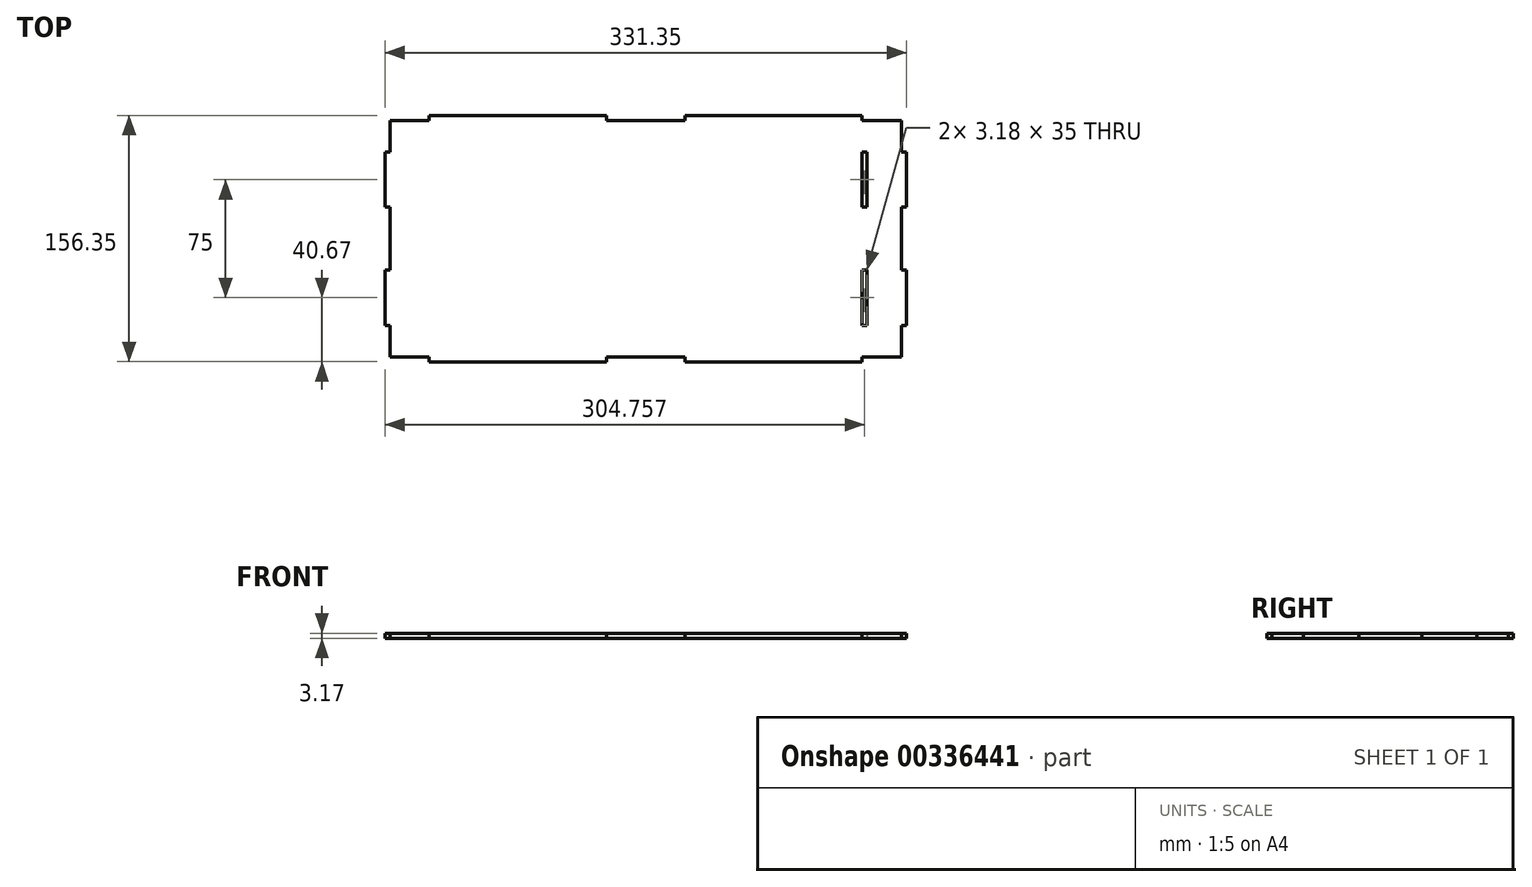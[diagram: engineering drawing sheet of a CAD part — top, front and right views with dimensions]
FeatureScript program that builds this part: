
annotation { "Feature Type Name" : "Feature", "Feature Type Description" : "" }
export const myFeature = defineFeature(function(context is Context, id is Id, definition is map)
    precondition{}
    {
        {
            var Q0;
            Q0=qCreatedBy(makeId("Top.planeOp"),FACE);
            var sketch = newSketch(context, id + "F0", { "sketchPlane" : qUnion([Q0])});
            skLineSegment(sketch, "E0", {"start": v(0, 0) * mm, "end": v(0, 150) * mm, "construction": true});
            skLineSegment(sketch, "E1", {"start": v(0, 150) * mm, "end": v(325, 150) * mm, "construction": true});
            skLineSegment(sketch, "E2", {"start": v(325, 150) * mm, "end": v(325, 0) * mm, "construction": true});
            skLineSegment(sketch, "E3", {"start": v(325, 0) * mm, "end": v(0, 0) * mm, "construction": true});
            skLineSegment(sketch, "E4", {"start": v(162.5, 150) * mm, "end": v(162.5, 0) * mm, "construction": true});
            skLineSegment(sketch, "E5", {"start": v(162.5, 0) * mm, "end": v(137.5, 0) * mm});
            skLineSegment(sketch, "E6", {"start": v(137.5, 0) * mm, "end": v(137.5, -3.18) * mm});
            skLineSegment(sketch, "E7", {"start": v(137.5, -3.18) * mm, "end": v(25, -3.18) * mm});
            skLineSegment(sketch, "E8", {"start": v(25, -3.18) * mm, "end": v(25, 0) * mm});
            skLineSegment(sketch, "E9", {"start": v(25, 0) * mm, "end": v(0, 0) * mm});
            skLineSegment(sketch, "E10", {"start": v(0, 20) * mm, "end": v(-3.18, 20) * mm});
            skLineSegment(sketch, "E11", {"start": v(-3.18, 20) * mm, "end": v(-3.18, 55) * mm});
            skLineSegment(sketch, "E12", {"start": v(-3.18, 55) * mm, "end": v(0, 55) * mm});
            skLineSegment(sketch, "E13", {"start": v(0, 75) * mm, "end": v(162.5, 75) * mm, "construction": true});
            skLineSegment(sketch, "E14.MirrorCS", {"start": v(0, 130) * mm, "end": v(-3.18, 130) * mm});
            skLineSegment(sketch, "E15.MirrorCS", {"start": v(-3.18, 95) * mm, "end": v(0, 95) * mm});
            skLineSegment(sketch, "E16.MirrorCS", {"start": v(137.5, 150) * mm, "end": v(137.5, 153.18) * mm});
            skLineSegment(sketch, "E17.MirrorCS", {"start": v(25, 153.18) * mm, "end": v(25, 150) * mm});
            skLineSegment(sketch, "E18.MirrorCS", {"start": v(25, 150) * mm, "end": v(0, 150) * mm});
            skLineSegment(sketch, "E19.MirrorCS", {"start": v(137.5, 153.18) * mm, "end": v(25, 153.18) * mm});
            skLineSegment(sketch, "E20.MirrorCS", {"start": v(-3.18, 130) * mm, "end": v(-3.18, 95) * mm});
            skLineSegment(sketch, "E21.MirrorCS", {"start": v(162.5, 150) * mm, "end": v(137.5, 150) * mm});
            skLineSegment(sketch, "E22", {"start": v(0, 95) * mm, "end": v(0, 55) * mm});
            skLineSegment(sketch, "E23", {"start": v(0, 150) * mm, "end": v(0, 130) * mm});
            skLineSegment(sketch, "E24", {"start": v(0, 20) * mm, "end": v(0, 0) * mm});
            skLineSegment(sketch, "E25.MirrorCS", {"start": v(187.5, 150) * mm, "end": v(187.5, 153.18) * mm});
            skLineSegment(sketch, "E26.MirrorCS", {"start": v(187.5, 0) * mm, "end": v(187.5, -3.18) * mm});
            skLineSegment(sketch, "E27.MirrorCS", {"start": v(300, -3.18) * mm, "end": v(300, 0) * mm});
            skLineSegment(sketch, "E28.MirrorCS", {"start": v(325, 20) * mm, "end": v(328.18, 20) * mm});
            skLineSegment(sketch, "E29.MirrorCS", {"start": v(300, 153.18) * mm, "end": v(300, 150) * mm});
            skLineSegment(sketch, "E30.MirrorCS", {"start": v(328.18, 55) * mm, "end": v(325, 55) * mm});
            skLineSegment(sketch, "E31.MirrorCS", {"start": v(328.18, 95) * mm, "end": v(325, 95) * mm});
            skLineSegment(sketch, "E32.MirrorCS", {"start": v(325, 130) * mm, "end": v(328.18, 130) * mm});
            skLineSegment(sketch, "E33.MirrorCS", {"start": v(300, 0) * mm, "end": v(325, 0) * mm});
            skLineSegment(sketch, "E34.MirrorCS", {"start": v(325, 20) * mm, "end": v(325, 0) * mm});
            skLineSegment(sketch, "E35.MirrorCS", {"start": v(187.5, -3.18) * mm, "end": v(300, -3.18) * mm});
            skLineSegment(sketch, "E36.MirrorCS", {"start": v(328.18, 20) * mm, "end": v(328.18, 55) * mm});
            skLineSegment(sketch, "E37.MirrorCS", {"start": v(162.5, 150) * mm, "end": v(187.5, 150) * mm});
            skLineSegment(sketch, "E38.MirrorCS", {"start": v(162.5, 0) * mm, "end": v(187.5, 0) * mm});
            skLineSegment(sketch, "E39.MirrorCS", {"start": v(187.5, 153.18) * mm, "end": v(300, 153.18) * mm});
            skLineSegment(sketch, "E40.MirrorCS", {"start": v(0, 0) * mm, "end": v(325, 0) * mm, "construction": true});
            skLineSegment(sketch, "E41.MirrorCS", {"start": v(325, 95) * mm, "end": v(325, 55) * mm});
            skLineSegment(sketch, "E42.MirrorCS", {"start": v(325, 75) * mm, "end": v(162.5, 75) * mm, "construction": true});
            skLineSegment(sketch, "E43.MirrorCS", {"start": v(325, 150) * mm, "end": v(0, 150) * mm, "construction": true});
            skLineSegment(sketch, "E44.MirrorCS", {"start": v(325, 150) * mm, "end": v(325, 130) * mm});
            skLineSegment(sketch, "E45.MirrorCS", {"start": v(300, 150) * mm, "end": v(325, 150) * mm});
            skLineSegment(sketch, "E46.MirrorCS", {"start": v(325, 0) * mm, "end": v(325, 150) * mm, "construction": true});
            skLineSegment(sketch, "E47.MirrorCS", {"start": v(328.18, 130) * mm, "end": v(328.18, 95) * mm});
            skLineSegment(sketch, "E48.1.0.0", {"start": v(303.17, 130) * mm, "end": v(303.17, 95) * mm});
            skLineSegment(sketch, "E48.1.0.2", {"start": v(303.17, 20) * mm, "end": v(303.17, 55) * mm});
            skLineSegment(sketch, "E48.1.0.3", {"start": v(300, 75) * mm, "end": v(137.5, 75) * mm, "construction": true});
            skLineSegment(sketch, "E48.1.0.4", {"start": v(300, 150) * mm, "end": v(300, 0) * mm, "construction": true});
            skLineSegment(sketch, "E48.1.0.6", {"start": v(300, 130) * mm, "end": v(303.18, 130) * mm});
            skLineSegment(sketch, "E48.1.0.7", {"start": v(300, 20) * mm, "end": v(300, 0) * mm, "construction": true});
            skLineSegment(sketch, "E48.1.0.8", {"start": v(303.18, 95) * mm, "end": v(300, 95) * mm});
            skLineSegment(sketch, "E48.1.0.10", {"start": v(300, 20) * mm, "end": v(303.18, 20) * mm});
            skLineSegment(sketch, "E48.1.0.11", {"start": v(303.18, 55) * mm, "end": v(300, 55) * mm});
            skLineSegment(sketch, "E48.direction1", {"start": v(162.5, 75) * mm, "end": v(137.5, 75) * mm, "construction": true});
            skLineSegment(sketch, "E49", {"start": v(300, 130) * mm, "end": v(300, 95) * mm});
            skLineSegment(sketch, "E50", {"start": v(300, 55) * mm, "end": v(300, 20) * mm});
            skSolve(sketch);
        }
        {
            var Q0;
            Q0=makeQuery(id+"F0.imprint","IMPRINT",FACE,{"disambiguationData":[TD([[makeQuery(id+"F0.imprint","IMPRINT",EDGE,{"derivedFrom":sQuery(id+"F0.wireOp",EDGE,"E5")}),-1.0]])]});
            extrude(context, id + "F1", {"entities" : qUnion([Q0]), "depth" : 3.17 * mm});
        }
    });
